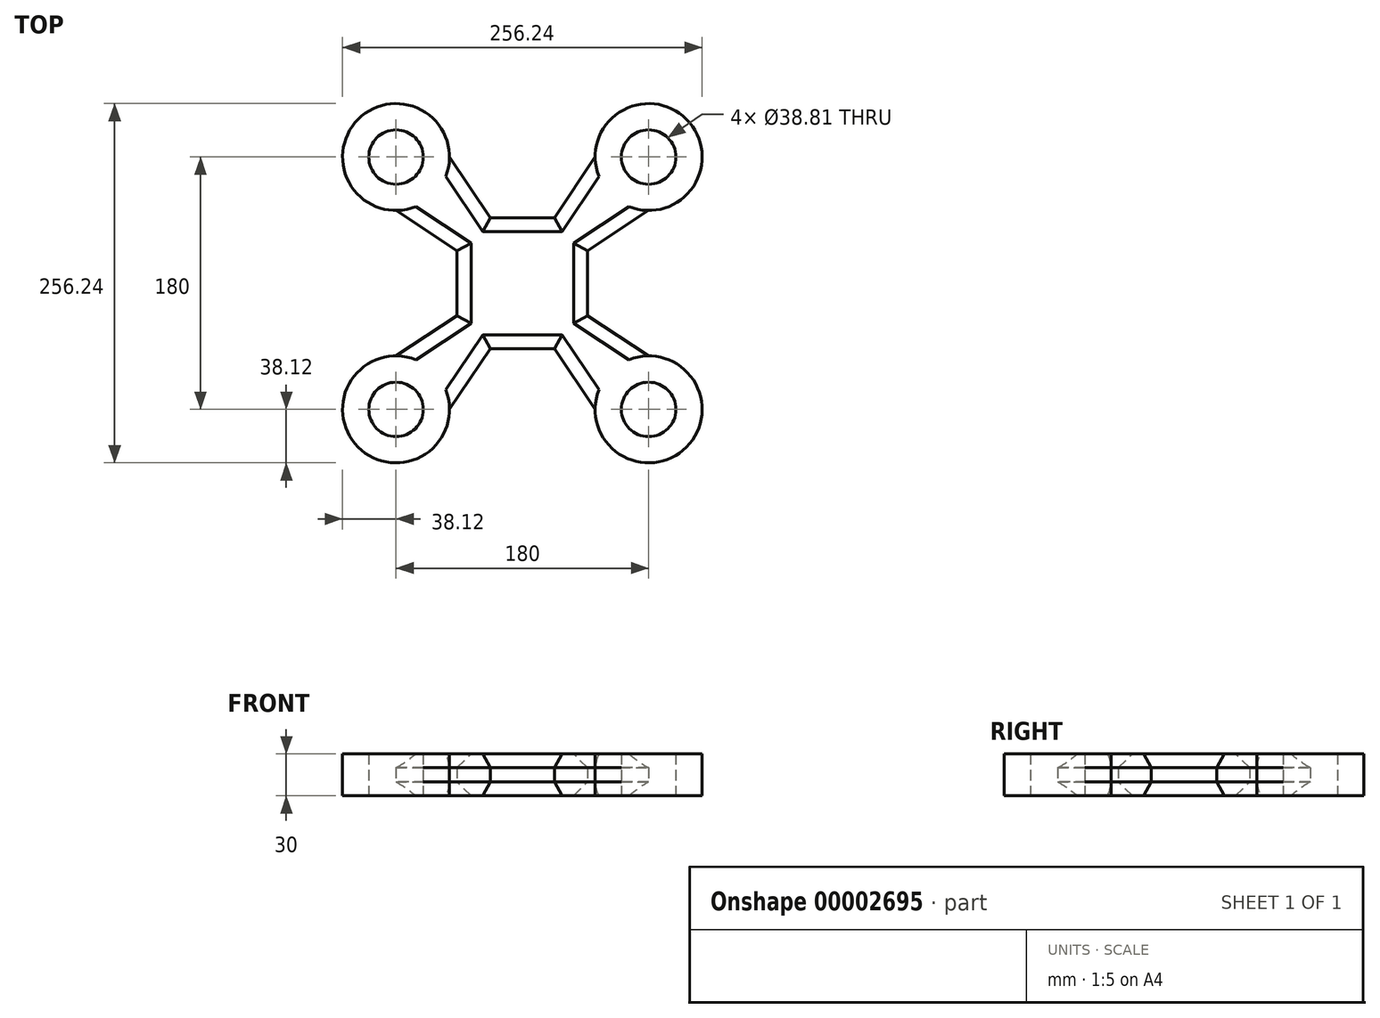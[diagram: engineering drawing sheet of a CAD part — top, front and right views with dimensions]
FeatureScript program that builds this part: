
annotation { "Feature Type Name" : "Feature", "Feature Type Description" : "" }
export const myFeature = defineFeature(function(context is Context, id is Id, definition is map)
    precondition{}
    {
        {
            var Q0;
            Q0=qCreatedBy(makeId("Top.planeOp"),FACE);
            var sketch = newSketch(context, id + "F0", { "sketchPlane" : qUnion([Q0])});
            skCircle(sketch, "E0", {"center": v(-90, 90) * mm, "radius": 38.12 * mm});
            skCircle(sketch, "E1", {"center": v(90, 90) * mm, "radius": 38.12 * mm});
            skCircle(sketch, "E2", {"center": v(-90, -90) * mm, "radius": 38.12 * mm});
            skCircle(sketch, "E3", {"center": v(90, -90) * mm, "radius": 38.12 * mm});
            skLineSegment(sketch, "E4", {"start": v(-90, 90) * mm, "end": v(90, 90) * mm, "construction": true});
            skLineSegment(sketch, "E5", {"start": v(90, 90) * mm, "end": v(90, -90) * mm, "construction": true});
            skLineSegment(sketch, "E6", {"start": v(90, -90) * mm, "end": v(-90, -90) * mm, "construction": true});
            skLineSegment(sketch, "E7", {"start": v(-90, -90) * mm, "end": v(-90, 90) * mm, "construction": true});
            skLineSegment(sketch, "E8", {"start": v(-90, 51.88) * mm, "end": v(-46.47, 23.26) * mm});
            skLineSegment(sketch, "E9", {"start": v(-46.47, 23.26) * mm, "end": v(-46.47, -23.26) * mm});
            skLineSegment(sketch, "E10", {"start": v(-46.47, -23.26) * mm, "end": v(-90, -51.88) * mm});
            skLineSegment(sketch, "E11", {"start": v(-51.88, 90) * mm, "end": v(-22.87, 46.73) * mm});
            skLineSegment(sketch, "E12", {"start": v(-22.87, 46.73) * mm, "end": v(22.87, 46.73) * mm});
            skLineSegment(sketch, "E13", {"start": v(22.87, 46.73) * mm, "end": v(51.88, 90) * mm});
            skLineSegment(sketch, "E14", {"start": v(90, 51.88) * mm, "end": v(46.47, 23.26) * mm});
            skLineSegment(sketch, "E15", {"start": v(46.47, 23.26) * mm, "end": v(46.47, -23.26) * mm});
            skLineSegment(sketch, "E16", {"start": v(46.47, -23.26) * mm, "end": v(90, -51.88) * mm});
            skLineSegment(sketch, "E17", {"start": v(-51.88, -90) * mm, "end": v(-22.87, -46.73) * mm});
            skLineSegment(sketch, "E18", {"start": v(-22.87, -46.73) * mm, "end": v(22.87, -46.73) * mm});
            skLineSegment(sketch, "E19", {"start": v(22.87, -46.73) * mm, "end": v(51.88, -90) * mm});
            skCircle(sketch, "E20", {"center": v(-90, 90) * mm, "radius": 19.4 * mm});
            skCircle(sketch, "E21", {"center": v(90, 90) * mm, "radius": 19.4 * mm});
            skCircle(sketch, "E22", {"center": v(90, -90) * mm, "radius": 19.4 * mm});
            skCircle(sketch, "E23", {"center": v(-90, -90) * mm, "radius": 19.4 * mm});
            skPoint(sketch, "E24", {"position": v(-46.47, 0) * mm});
            skPoint(sketch, "E25", {"position": v(0, 46.73) * mm});
            skPoint(sketch, "E26", {"position": v(46.47, 0) * mm});
            skSolve(sketch);
        }
        {
            var Q0;
            Q0 = qSketchRegion(id + "F0", true);
            extrude(context, id + "F1", {"entities" : qUnion([Q0]), "depth" : 30 * mm});
        }
        {
            var Q0;
            Q0=makeQuery(id+"F1.opExtrude","CAP_EDGE",EDGE,{"disambiguationData":[OSD([sQuery(id+"F0.wireOp",EDGE,"E9")])],"isStart":false});
            var Q1;
            Q1=makeQuery(id+"F1.opExtrude","CAP_EDGE",EDGE,{"disambiguationData":[OSD([sQuery(id+"F0.wireOp",EDGE,"E11")])],"isStart":false});
            var Q2;
            Q2=makeQuery(id+"F1.opExtrude","CAP_EDGE",EDGE,{"disambiguationData":[OSD([sQuery(id+"F0.wireOp",EDGE,"E12")])],"isStart":false});
            var Q3;
            Q3=makeQuery(id+"F1.opExtrude","CAP_EDGE",EDGE,{"disambiguationData":[OSD([sQuery(id+"F0.wireOp",EDGE,"E13")])],"isStart":false});
            var Q4;
            Q4=makeQuery(id+"F1.opExtrude","CAP_EDGE",EDGE,{"disambiguationData":[OSD([sQuery(id+"F0.wireOp",EDGE,"E14")])],"isStart":false});
            var Q5;
            Q5=makeQuery(id+"F1.opExtrude","CAP_EDGE",EDGE,{"disambiguationData":[OSD([sQuery(id+"F0.wireOp",EDGE,"E15")])],"isStart":false});
            var Q6;
            Q6=makeQuery(id+"F1.opExtrude","CAP_EDGE",EDGE,{"disambiguationData":[OSD([sQuery(id+"F0.wireOp",EDGE,"E16")])],"isStart":false});
            var Q7;
            Q7=makeQuery(id+"F1.opExtrude","CAP_EDGE",EDGE,{"disambiguationData":[OSD([sQuery(id+"F0.wireOp",EDGE,"E19")])],"isStart":false});
            var Q8;
            Q8=makeQuery(id+"F1.opExtrude","CAP_EDGE",EDGE,{"disambiguationData":[OSD([sQuery(id+"F0.wireOp",EDGE,"E18")])],"isStart":false});
            var Q9;
            Q9=makeQuery(id+"F1.opExtrude","CAP_EDGE",EDGE,{"disambiguationData":[OSD([sQuery(id+"F0.wireOp",EDGE,"E17")])],"isStart":false});
            var Q10;
            Q10=makeQuery(id+"F1.opExtrude","CAP_EDGE",EDGE,{"disambiguationData":[OSD([sQuery(id+"F0.wireOp",EDGE,"E10")])],"isStart":false});
            var Q11;
            Q11=makeQuery(id+"F1.opExtrude","CAP_EDGE",EDGE,{"disambiguationData":[OSD([sQuery(id+"F0.wireOp",EDGE,"E8")])],"isStart":false});
            var Q12;
            Q12=makeQuery(id+"F1.opExtrude","CAP_EDGE",EDGE,{"disambiguationData":[OSD([sQuery(id+"F0.wireOp",EDGE,"E19")])],"isStart":true});
            var Q13;
            Q13=makeQuery(id+"F1.opExtrude","CAP_EDGE",EDGE,{"disambiguationData":[OSD([sQuery(id+"F0.wireOp",EDGE,"E18")])],"isStart":true});
            var Q14;
            Q14=makeQuery(id+"F1.opExtrude","CAP_EDGE",EDGE,{"disambiguationData":[OSD([sQuery(id+"F0.wireOp",EDGE,"E17")])],"isStart":true});
            var Q15;
            Q15=makeQuery(id+"F1.opExtrude","CAP_EDGE",EDGE,{"disambiguationData":[OSD([sQuery(id+"F0.wireOp",EDGE,"E10")])],"isStart":true});
            var Q16;
            Q16=makeQuery(id+"F1.opExtrude","CAP_EDGE",EDGE,{"disambiguationData":[OSD([sQuery(id+"F0.wireOp",EDGE,"E9")])],"isStart":true});
            var Q17;
            Q17=makeQuery(id+"F1.opExtrude","CAP_EDGE",EDGE,{"disambiguationData":[OSD([sQuery(id+"F0.wireOp",EDGE,"E8")])],"isStart":true});
            var Q18;
            Q18=makeQuery(id+"F1.opExtrude","CAP_EDGE",EDGE,{"disambiguationData":[OSD([sQuery(id+"F0.wireOp",EDGE,"E11")])],"isStart":true});
            var Q19;
            Q19=makeQuery(id+"F1.opExtrude","CAP_EDGE",EDGE,{"disambiguationData":[OSD([sQuery(id+"F0.wireOp",EDGE,"E12")])],"isStart":true});
            var Q20;
            Q20=makeQuery(id+"F1.opExtrude","CAP_EDGE",EDGE,{"disambiguationData":[OSD([sQuery(id+"F0.wireOp",EDGE,"E13")])],"isStart":true});
            var Q21;
            Q21=makeQuery(id+"F1.opExtrude","CAP_EDGE",EDGE,{"disambiguationData":[OSD([sQuery(id+"F0.wireOp",EDGE,"E14")])],"isStart":true});
            var Q22;
            Q22=makeQuery(id+"F1.opExtrude","CAP_EDGE",EDGE,{"disambiguationData":[OSD([sQuery(id+"F0.wireOp",EDGE,"E15")])],"isStart":true});
            var Q23;
            Q23=makeQuery(id+"F1.opExtrude","CAP_EDGE",EDGE,{"disambiguationData":[OSD([sQuery(id+"F0.wireOp",EDGE,"E16")])],"isStart":true});
            chamfer(context, id + "F2", {"entities" : qUnion([Q0, Q1, Q2, Q3, Q4, Q5, Q6, Q7, Q8, Q9, Q10, Q11, Q12, Q13, Q14, Q15, Q16, Q17, Q18, Q19, Q20, Q21, Q22, Q23]), "width" : 10 * mm, "tangentPropagation" : true});
        }
    });
